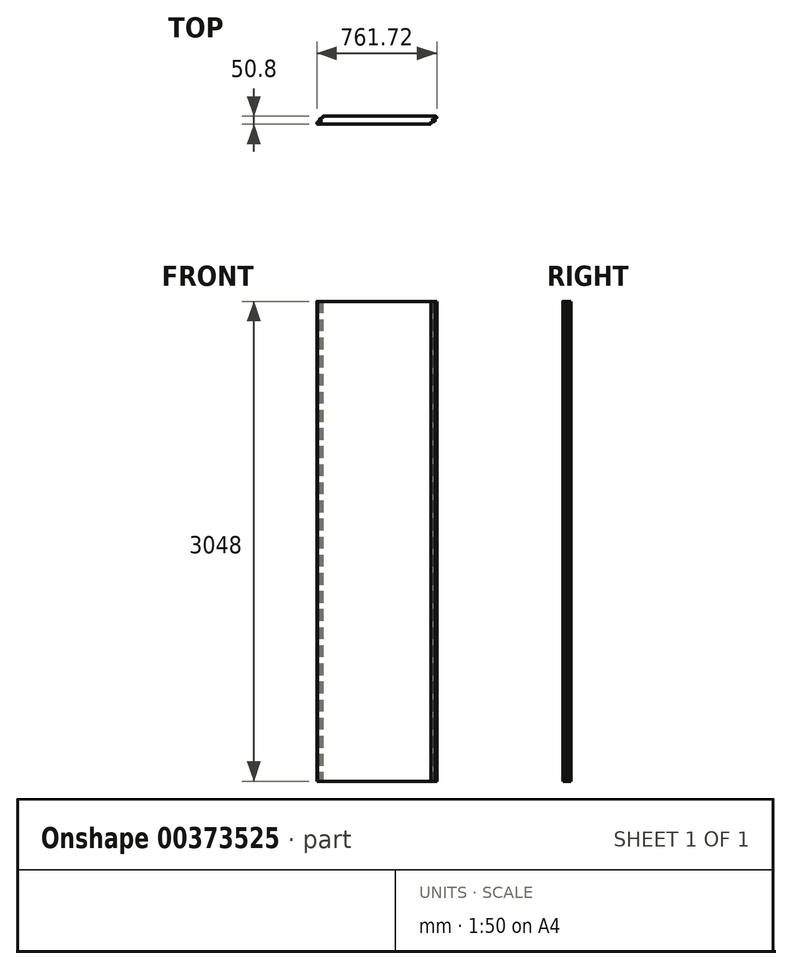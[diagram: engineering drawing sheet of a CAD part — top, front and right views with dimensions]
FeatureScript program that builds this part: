
annotation { "Feature Type Name" : "Feature", "Feature Type Description" : "" }
export const myFeature = defineFeature(function(context is Context, id is Id, definition is map)
    precondition{}
    {
        {
            var Q0;
            Q0=qCreatedBy(makeId("Top.planeOp"),FACE);
            var sketch = newSketch(context, id + "F0", { "sketchPlane" : qUnion([Q0])});
            skLineSegment(sketch, "E0.bottom", {"start": v(-339.23, 25.4) * mm, "end": v(375.68, 25.4) * mm});
            skLineSegment(sketch, "E0.top", {"start": v(-375.68, -25.4) * mm, "end": v(339.23, -25.4) * mm});
            skArc(sketch, "E1", {"start": v(-375.5, -10.35) * mm, "mid": v(-380.85, -17.8) * mm, "end": v(-375.68, -25.4) * mm});
            skLineSegment(sketch, "E2", {"start": v(-375.5, -10.35) * mm, "end": v(-354.32, -10.35) * mm});
            skLineSegment(sketch, "E3", {"start": v(-354.32, -10.35) * mm, "end": v(-354.32, -1.3) * mm});
            skLineSegment(sketch, "E4", {"start": v(-354.32, -1.3) * mm, "end": v(-359.68, -1.3) * mm});
            skArc(sketch, "E5", {"start": v(-359.68, 10.23) * mm, "mid": v(-365.44, 4.47) * mm, "end": v(-359.68, -1.3) * mm});
            skLineSegment(sketch, "E6", {"start": v(-359.68, 10.23) * mm, "end": v(-345.58, 10.23) * mm});
            skLineSegment(sketch, "E7", {"start": v(-345.58, 10.23) * mm, "end": v(-345.58, 19.05) * mm});
            skArc(sketch, "E8.filletArc", {"start": v(-339.23, 25.4) * mm, "mid": v(-343.72, 23.54) * mm, "end": v(-345.58, 19.05) * mm});
            skArc(sketch, "E9.MirrorCS", {"start": v(375.5, 10.35) * mm, "mid": v(380.85, 17.8) * mm, "end": v(375.68, 25.4) * mm});
            skLineSegment(sketch, "E10.MirrorCS", {"start": v(375.5, 10.35) * mm, "end": v(354.32, 10.35) * mm});
            skLineSegment(sketch, "E11.MirrorCS", {"start": v(354.32, 10.35) * mm, "end": v(354.32, 1.3) * mm});
            skLineSegment(sketch, "E12.MirrorCS", {"start": v(354.32, 1.3) * mm, "end": v(364.28, 1.3) * mm});
            skArc(sketch, "E13.MirrorCS", {"start": v(339.23, -25.4) * mm, "mid": v(343.72, -23.54) * mm, "end": v(345.58, -19.05) * mm});
            skLineSegment(sketch, "E14.MirrorCS", {"start": v(364.28, -9.02) * mm, "end": v(345.58, -9.02) * mm});
            skLineSegment(sketch, "E15.MirrorCS", {"start": v(345.58, -9.02) * mm, "end": v(345.58, -19.05) * mm});
            skArc(sketch, "E16.MirrorCS", {"start": v(364.28, -9.02) * mm, "mid": v(369.44, -3.86) * mm, "end": v(364.28, 1.3) * mm});
            skSolve(sketch);
        }
        {
            var Q0;
            Q0=makeQuery(id+"F0.imprint","IMPRINT",FACE,{"disambiguationData":[TD([[makeQuery(id+"F0.imprint","IMPRINT",EDGE,{"derivedFrom":sQuery(id+"F0.wireOp",EDGE,"E0.bottom")}),-1.0]])]});
            extrude(context, id + "F1", {"entities" : qUnion([Q0]), "depth" : 3048 * mm});
        }
    });
